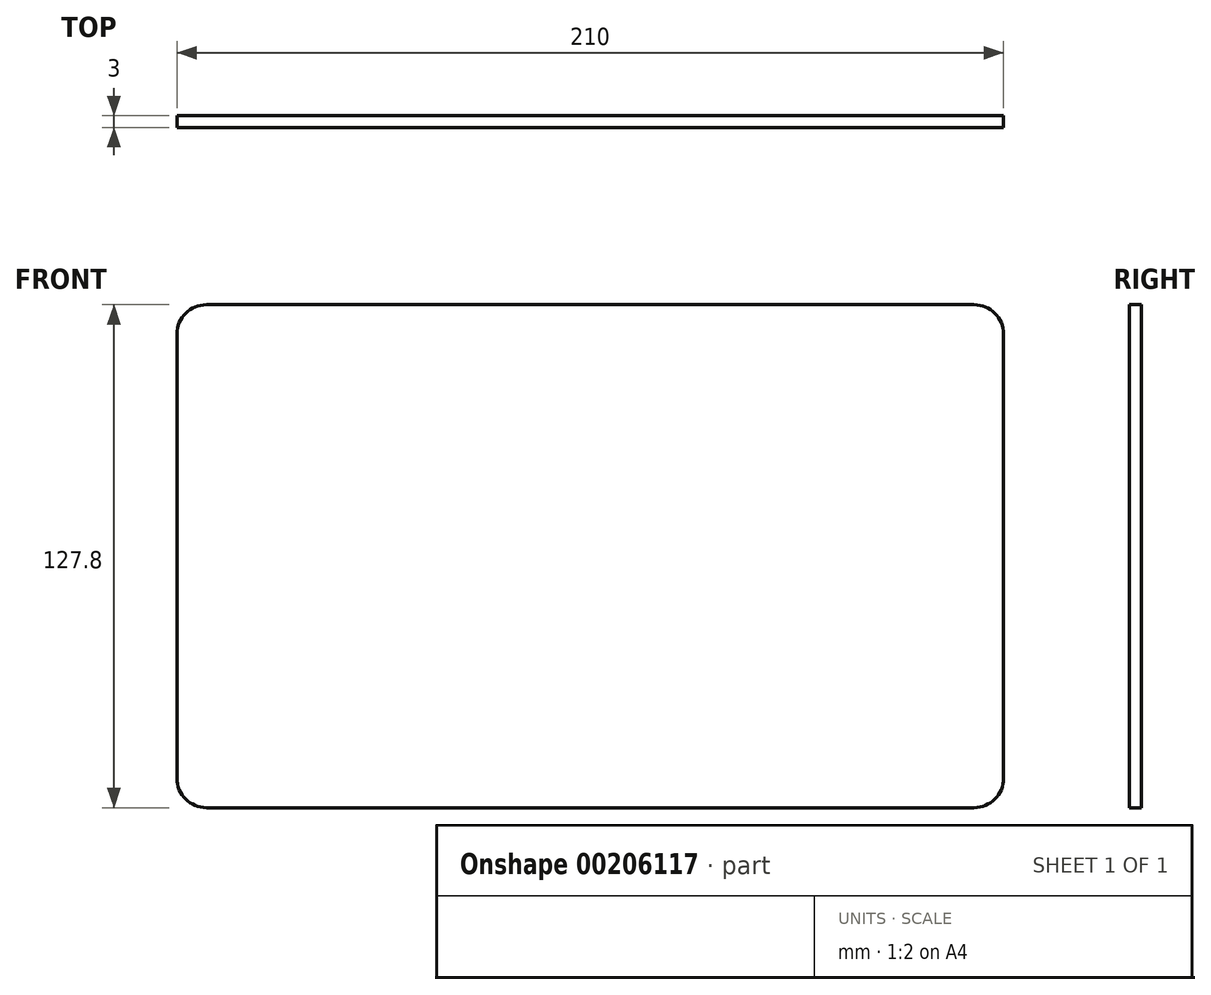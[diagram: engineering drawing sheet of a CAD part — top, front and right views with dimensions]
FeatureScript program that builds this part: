
annotation { "Feature Type Name" : "Feature", "Feature Type Description" : "" }
export const myFeature = defineFeature(function(context is Context, id is Id, definition is map)
    precondition{}
    {
        {
            var Q0;
            Q0=qCreatedBy(makeId("Front.planeOp"),FACE);
            var sketch = newSketch(context, id + "F0", { "sketchPlane" : qUnion([Q0])});
            skPoint(sketch, "E0.middle", {"position": v(0, 0) * mm});
            skLineSegment(sketch, "E1.bottom", {"start": v(97.5, 63.9) * mm, "end": v(-97.5, 63.9) * mm});
            skLineSegment(sketch, "E1.top", {"start": v(97.5, -63.9) * mm, "end": v(-97.5, -63.9) * mm});
            skLineSegment(sketch, "E1.left", {"start": v(105, 56.4) * mm, "end": v(105, -56.4) * mm});
            skLineSegment(sketch, "E1.right", {"start": v(-105, 56.4) * mm, "end": v(-105, -56.4) * mm});
            skPoint(sketch, "E2.visualSharp", {"position": v(-105, -63.9) * mm});
            skArc(sketch, "E2.filletArc", {"start": v(-105, -56.4) * mm, "mid": v(-102.8, -61.7) * mm, "end": v(-97.5, -63.9) * mm});
            skPoint(sketch, "E3.visualSharp", {"position": v(105, -63.9) * mm});
            skArc(sketch, "E3.filletArc", {"start": v(97.5, -63.9) * mm, "mid": v(102.8, -61.7) * mm, "end": v(105, -56.4) * mm});
            skPoint(sketch, "E4.visualSharp", {"position": v(105, 63.9) * mm});
            skArc(sketch, "E4.filletArc", {"start": v(105, 56.4) * mm, "mid": v(102.8, 61.7) * mm, "end": v(97.5, 63.9) * mm});
            skPoint(sketch, "E5.visualSharp", {"position": v(-105, 63.9) * mm});
            skArc(sketch, "E5.filletArc", {"start": v(-97.5, 63.9) * mm, "mid": v(-102.8, 61.7) * mm, "end": v(-105, 56.4) * mm});
            skLineSegment(sketch, "E6", {"start": v(0, 55.38) * mm, "end": v(0, 48.75) * mm, "construction": true});
            skPoint(sketch, "E6.endSnap0", {"position": v(0, 55.38) * mm});
            skLineSegment(sketch, "E7", {"start": v(0, 0) * mm, "end": v(0, -51.85) * mm, "construction": true});
            skPoint(sketch, "E7.endSnap0", {"position": v(0, -55.38) * mm});
            skPoint(sketch, "E8.middle", {"position": v(0, -1.55) * mm});
            skPoint(sketch, "E0.left.end.orphan", {"position": v(96.48, 55.38) * mm});
            skPoint(sketch, "E9.orphan", {"position": v(96.48, -55.38) * mm});
            skPoint(sketch, "E0.right.end.orphan", {"position": v(-96.48, 55.38) * mm});
            skPoint(sketch, "E0.right.start.orphan", {"position": v(-96.48, -55.38) * mm});
            skPoint(sketch, "E8.left.start.orphan", {"position": v(83.1, 48.75) * mm});
            skPoint(sketch, "E10.orphan", {"position": v(83.1, -51.85) * mm});
            skPoint(sketch, "E8.right.end.orphan", {"position": v(-83.1, -51.85) * mm});
            skPoint(sketch, "E11.left.start.orphan", {"position": v(-83.1, 48.75) * mm});
            skSolve(sketch);
        }
        {
            var Q0;
            Q0=makeQuery(id+"F0.imprint","IMPRINT",FACE,{"disambiguationData":[TD([[makeQuery(id+"F0.imprint","IMPRINT",EDGE,{"derivedFrom":sQuery(id+"F0.wireOp",EDGE,"E0.bottom")}),1.0]])]});
            var Q1;
            Q1=makeQuery(id+"F0.imprint","IMPRINT",FACE,{"disambiguationData":[TD([[makeQuery(id+"F0.imprint","IMPRINT",EDGE,{"derivedFrom":sQuery(id+"F0.wireOp",EDGE,"E0.bottom")}),-1.0]])]});
            var Q2;
            Q2=makeQuery(id+"F0.imprint","IMPRINT",FACE,{"disambiguationData":[TD([[makeQuery(id+"F0.imprint","IMPRINT",EDGE,{"derivedFrom":sQuery(id+"F0.wireOp",EDGE,"E1.bottom")}),1.0]])]});
            extrude(context, id + "F1", {"entities" : qUnion([Q0, Q1, Q2]), "depth" : 3 * mm});
        }
    });
